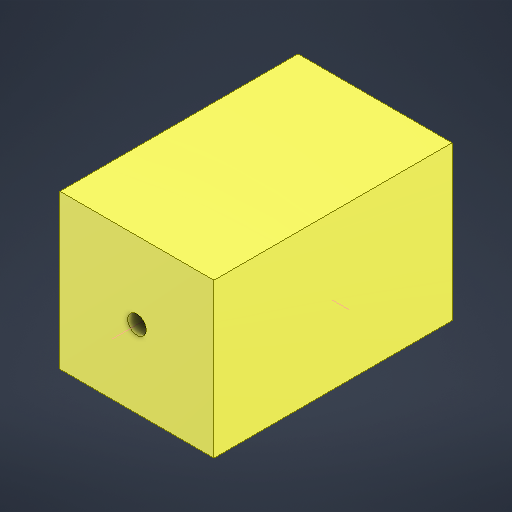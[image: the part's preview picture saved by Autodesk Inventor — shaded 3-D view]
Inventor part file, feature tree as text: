
AUTODESK INVENTOR PART (.ipt)
format: ipt  version: 2025.3 (Build 293356030, 356C)  size: 184,832 bytes
history: native  units: mm
features: extrude x1, sketch x1
ambient origin geometry x8: Origin, YZ Plane, XZ Plane, XY Plane, X Axis, Y Axis, Z Axis, Center Point
bodies: Body1 (feature_tree)
feature tree (2):
  extrude  "擠出6"  Depth=220.0mm
  sketch  "草圖5"
